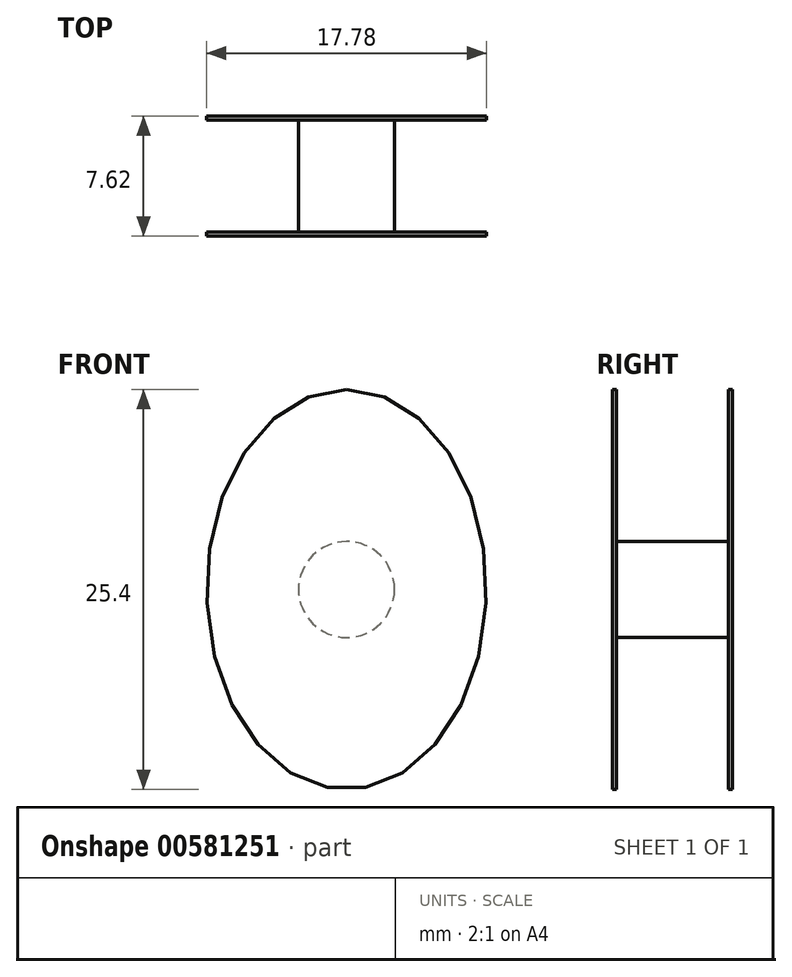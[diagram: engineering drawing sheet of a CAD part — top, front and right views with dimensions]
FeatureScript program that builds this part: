
annotation { "Feature Type Name" : "Feature", "Feature Type Description" : "" }
export const myFeature = defineFeature(function(context is Context, id is Id, definition is map)
    precondition{}
    {
        {
            var Q0;
            Q0=qCreatedBy(makeId("Front.planeOp"),FACE);
            var sketch = newSketch(context, id + "F0", { "sketchPlane" : qUnion([Q0])});
            skCircle(sketch, "E0", {"center": v(0, 0) * mm, "radius": 3.05 * mm});
            skSolve(sketch);
        }
        {
            var Q0;
            Q0=makeQuery(id+"F0.imprint","IMPRINT",FACE,{"disambiguationData":[TD([[makeQuery(id+"F0.imprint","IMPRINT",EDGE,{"derivedFrom":sQuery(id+"F0.wireOp",EDGE,"E0")}),1.0]])]});
            var Q1;
            Q1=sQuery(id+"F0.wireOp",EDGE,"E0");
            extrude(context, id + "F1", {"entities" : qUnion([Q0]), "surfaceEntities" : qUnion([Q1]), "depth" : 3.8 * mm, "offsetDistance" : 25.4 * mm});
        }
        {
            var Q0;
            Q0=makeQuery(id+"F1.opExtrude","CAP_FACE",FACE,{"disambiguationData":[OSD([sQuery(id+"F0.wireOp",EDGE,"E0")])],"isStart":false});
            var sketch = newSketch(context, id + "F2", { "sketchPlane" : qUnion([Q0])});
            skEllipse(sketch, "E1", {"center": v(0, 0) * mm, "majorRadius": 12.7 * mm, "minorRadius": 8.9 * mm, "majorAxis": v(0, 1)});
            skSolve(sketch);
        }
        {
            var Q0;
            Q0=makeQuery(id+"F2.imprint","IMPRINT",FACE,{"disambiguationData":[TD([[makeQuery(id+"F2.imprint","IMPRINT",EDGE,{"derivedFrom":sQuery(id+"F2.wireOp",EDGE,"E1")}),1.0]])]});
            var Q1;
            Q1=sQuery(id+"F2.wireOp",EDGE,"E1");
            extrude(context, id + "F3", {"entities" : qUnion([Q0]), "operationType" : NewBodyOperationType.ADD, "surfaceEntities" : qUnion([Q1]), "oppositeDirection" : true, "depth" : 0.25 * mm, "offsetDistance" : 25.4 * mm});
        }
        {
            var Q0;
            Q0=makeQuery(id+"F1.opExtrude","SWEPT_BODY",BODY,{"disambiguationData":[OSD([sQuery(id+"F0.wireOp",EDGE,"E0")])]});
            var Q1;
            Q1=qCreatedBy(makeId("Front.planeOp"),FACE);
            mirror(context, id + "F4", {"operationType" : NewBodyOperationType.ADD, "entities" : qUnion([Q0]), "mirrorPlane" : qUnion([Q1])});
        }
    });
